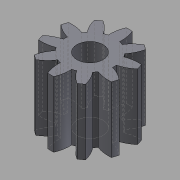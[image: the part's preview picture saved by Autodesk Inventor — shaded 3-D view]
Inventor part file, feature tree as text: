
AUTODESK INVENTOR PART (.ipt)
format: ipt  version: 2015 (Build 190159000, 159)  size: 173,056 bytes
history: native  units: in
note: dims shown in document units (in); Inventor stores cm internally (conversion verified against a paired STEP export)
features: other x13, sketch x3, plane x2
ambient origin geometry x8: Origin, YZ Plane, XZ Plane, XY Plane, X Axis, Y Axis, Z Axis, Center Point
bodies: Solid1 (feature_tree)
feature tree (18):
  other  "Spur Gear14_MIR3.ipt"
  other  "Solid1::Spur Gear14_MIR3.ipt"
  other  "TaggingFeature1"
  sketch  "Sketch1"  dims[d0=0.3937in]
  sketch  "Sketch2"  dims[d16=0.4724in d17=0.0in d41=0.0in d43=0.4724in d46=0.4724in d47=0.0in d48=0.0in]
  sketch  "Sketch3"
  plane  "XZ Plane_1"
  plane  "Work Plane2"
  other  "Z Axis_1"
  other  "Srf1"
  other  "Srf1::Derived"
  other  "Distance iMate"
  other  "Align iMate"
  other  "Mesh iMate"
  other  "Axis iMate"
  other  "Position iMate"
  other  "Mesh iMate2"
  other  "Start plane iMate"
